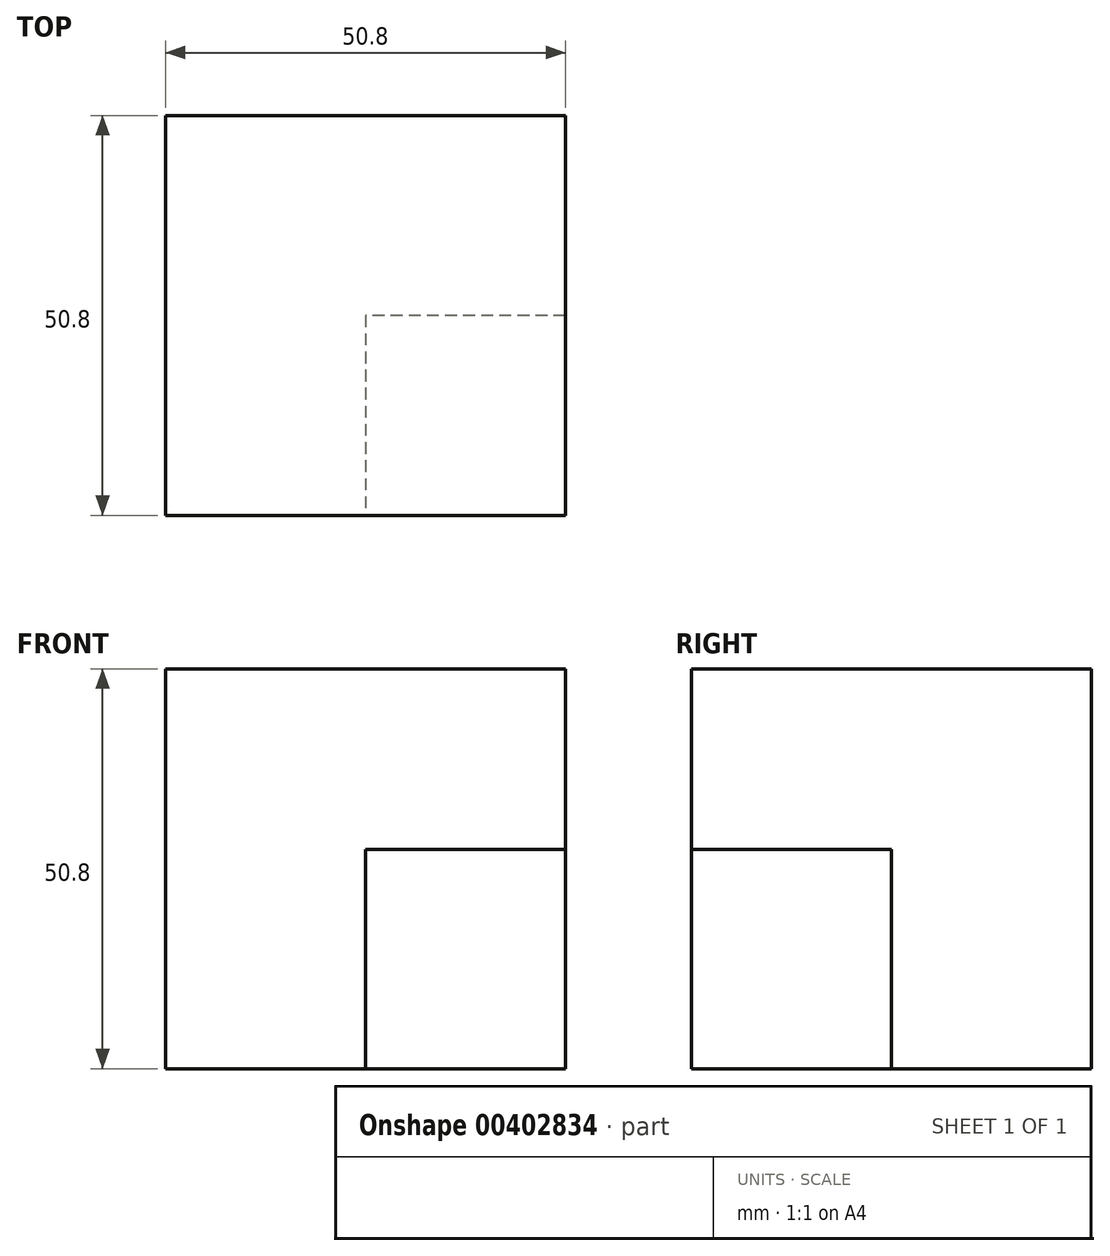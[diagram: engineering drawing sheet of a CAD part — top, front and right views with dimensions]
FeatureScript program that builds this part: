
annotation { "Feature Type Name" : "Feature", "Feature Type Description" : "" }
export const myFeature = defineFeature(function(context is Context, id is Id, definition is map)
    precondition{}
    {
        {
            var Q0;
            Q0=qCreatedBy(makeId("Front.planeOp"),FACE);
            var sketch = newSketch(context, id + "F0", { "sketchPlane" : qUnion([Q0])});
            skLineSegment(sketch, "E0", {"start": v(-29.14, 22.94) * mm, "end": v(-29.14, -27.86) * mm});
            skLineSegment(sketch, "E1", {"start": v(-29.14, 22.94) * mm, "end": v(21.66, 22.94) * mm});
            skLineSegment(sketch, "E2", {"start": v(21.66, 22.94) * mm, "end": v(21.66, -27.86) * mm});
            skLineSegment(sketch, "E3", {"start": v(21.66, -27.86) * mm, "end": v(-29.14, -27.86) * mm});
            skSolve(sketch);
        }
        {
            var Q0;
            Q0 = qSketchRegion(id + "F0", true);
            extrude(context, id + "F1", {"entities" : qUnion([Q0]), "depth" : 50.8 * mm});
        }
        {
            var Q0;
            Q0=qCreatedBy(makeId("Front.planeOp"),FACE);
            var sketch = newSketch(context, id + "F2", { "sketchPlane" : qUnion([Q0])});
            skLineSegment(sketch, "E4", {"start": v(25.4, -28.05) * mm, "end": v(0, -28.05) * mm});
            skLineSegment(sketch, "E5", {"start": v(0, -28.05) * mm, "end": v(0, -2.65) * mm});
            skLineSegment(sketch, "E6", {"start": v(0, -2.65) * mm, "end": v(21.43, -2.65) * mm});
            skLineSegment(sketch, "E7", {"start": v(21.43, -2.65) * mm, "end": v(21.43, -28.05) * mm});
            skLineSegment(sketch, "E8", {"start": v(21.43, -28.05) * mm, "end": v(21.43, -2.65) * mm});
            skSolve(sketch);
        }
        {
            var Q0;
            Q0 = qSketchRegion(id + "F2", true);
            extrude(context, id + "F3", {"entities" : qUnion([Q0]), "operationType" : NewBodyOperationType.REMOVE, "oppositeDirection" : true, "depth" : 25.4 * mm});
        }
        {
            var Q0;
            Q0=makeQuery(id+"F1.opExtrude","CAP_FACE",FACE,{"disambiguationData":[OSD([sQuery(id+"F0.wireOp",EDGE,"E0"),sQuery(id+"F0.wireOp",EDGE,"E1"),sQuery(id+"F0.wireOp",EDGE,"E2"),sQuery(id+"F0.wireOp",EDGE,"E3")])],"isStart":false});
            var sketch = newSketch(context, id + "F4", { "sketchPlane" : qUnion([Q0])});
            skLineSegment(sketch, "E9", {"start": v(-3.74, -27.86) * mm, "end": v(-3.74, 0) * mm});
            skLineSegment(sketch, "E10", {"start": v(-3.74, 0) * mm, "end": v(21.66, 0) * mm});
            skLineSegment(sketch, "E11", {"start": v(-3.74, -27.86) * mm, "end": v(21.66, -27.86) * mm});
            skLineSegment(sketch, "E12", {"start": v(21.66, -27.86) * mm, "end": v(21.66, 0) * mm});
            skSolve(sketch);
        }
        {
            var Q0;
            Q0 = qSketchRegion(id + "F4", true);
            extrude(context, id + "F5", {"entities" : qUnion([Q0]), "operationType" : NewBodyOperationType.REMOVE, "oppositeDirection" : true, "depth" : 25.4 * mm});
        }
    });
